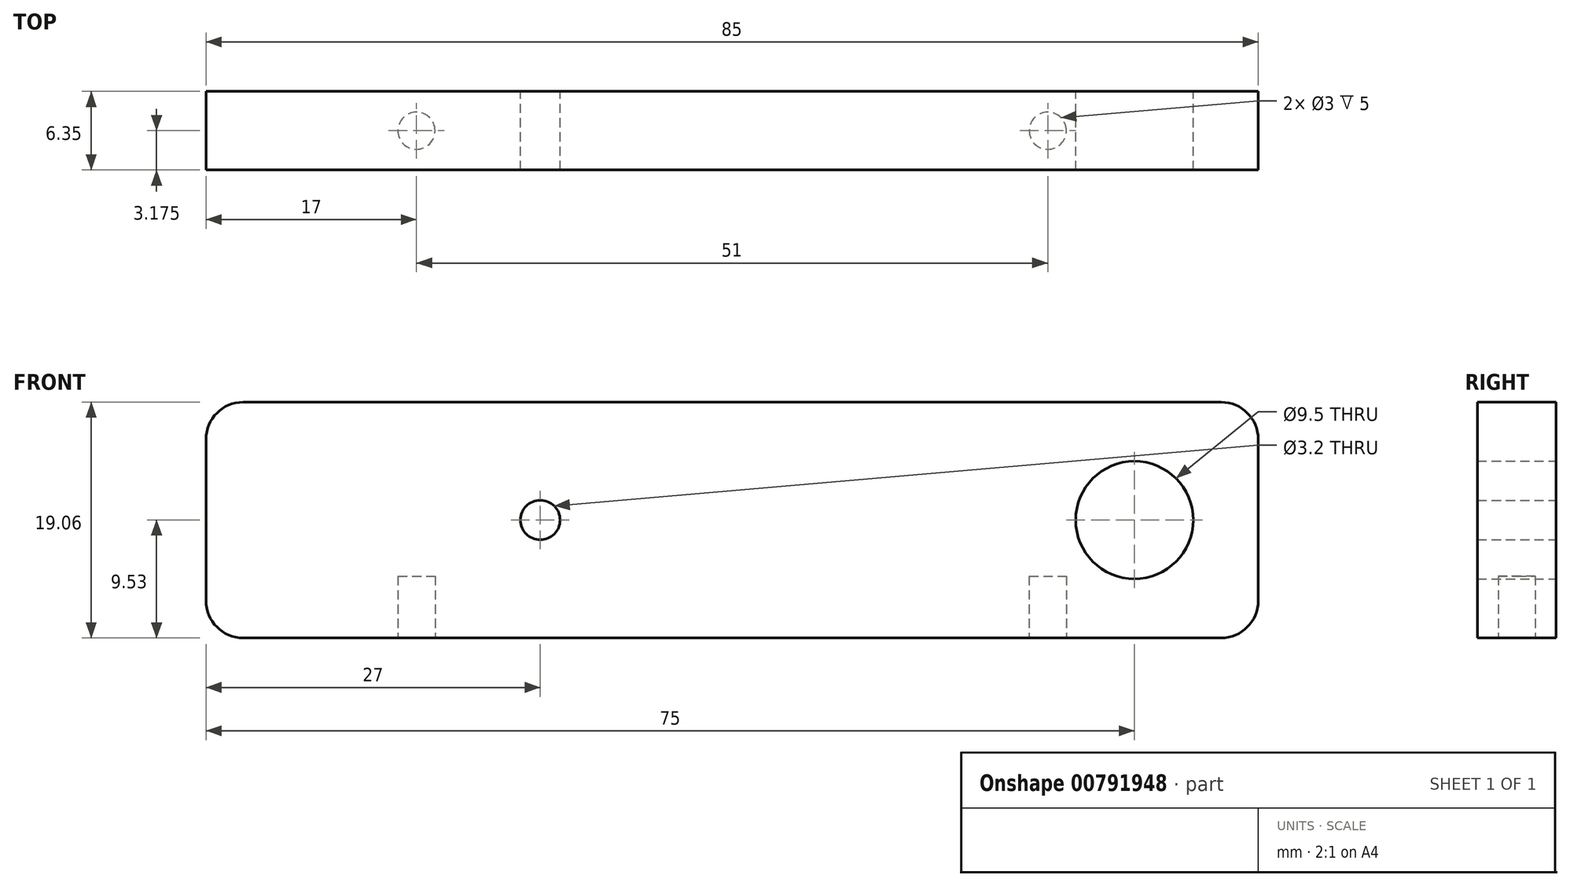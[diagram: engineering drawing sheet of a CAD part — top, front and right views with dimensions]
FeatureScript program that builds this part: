
annotation { "Feature Type Name" : "Feature", "Feature Type Description" : "" }
export const myFeature = defineFeature(function(context is Context, id is Id, definition is map)
    precondition{}
    {
        {
            var Q0;
            Q0=qCreatedBy(makeId("Front.planeOp"),FACE);
            var sketch = newSketch(context, id + "F0", { "sketchPlane" : qUnion([Q0])});
            skLineSegment(sketch, "E0.bottom", {"start": v(42.5, 9.53) * mm, "end": v(-42.5, 9.53) * mm});
            skLineSegment(sketch, "E0.top", {"start": v(42.5, -9.53) * mm, "end": v(-42.5, -9.53) * mm});
            skLineSegment(sketch, "E0.left", {"start": v(42.5, 9.53) * mm, "end": v(42.5, -9.53) * mm});
            skLineSegment(sketch, "E0.right", {"start": v(-42.5, 9.53) * mm, "end": v(-42.5, -9.53) * mm});
            skPoint(sketch, "E0.middle", {"position": v(0, 0) * mm});
            skCircle(sketch, "E1", {"center": v(32.5, 0) * mm, "radius": 4.75 * mm});
            skCircle(sketch, "E2", {"center": v(-15.5, 0) * mm, "radius": 1.6 * mm});
            skSolve(sketch);
        }
        {
            var Q0;
            Q0 = qSketchRegion(id + "F0", true);
            extrude(context, id + "F1", {"entities" : qUnion([Q0]), "depth" : 6.35 * mm, "offsetDistance" : 25 * mm});
        }
        {
            var Q0;
            Q0=makeQuery(id+"F1.opExtrude","SWEPT_FACE",FACE,{"disambiguationData":[OSD([sQuery(id+"F0.wireOp",EDGE,"E0.top")])]});
            var sketch = newSketch(context, id + "F2", { "sketchPlane" : qUnion([Q0])});
            skCircle(sketch, "E3", {"center": v(-25.5, 3.18) * mm, "radius": 1.5 * mm});
            skPoint(sketch, "E3.centerSnap0", {"position": v(-42.5, 3.17) * mm});
            skCircle(sketch, "E4.MirrorC", {"center": v(25.5, 3.18) * mm, "radius": 1.5 * mm});
            skSolve(sketch);
        }
        {
            var Q0;
            Q0 = qSketchRegion(id + "F2", true);
            extrude(context, id + "F3", {"entities" : qUnion([Q0]), "operationType" : NewBodyOperationType.REMOVE, "oppositeDirection" : true, "depth" : 5 * mm, "offsetDistance" : 25 * mm});
        }
        {
            var Q0;
            Q0=makeQuery(id+"F1.opExtrude","SWEPT_EDGE",EDGE,{"disambiguationData":[OSD([sQuery(id+"F0.wireOp",EDGE,"E0.top"),sQuery(id+"F0.wireOp",EDGE,"E0.right")])]});
            var Q1;
            Q1=makeQuery(id+"F1.opExtrude","SWEPT_EDGE",EDGE,{"disambiguationData":[OSD([sQuery(id+"F0.wireOp",EDGE,"E0.top"),sQuery(id+"F0.wireOp",EDGE,"E0.left")])]});
            var Q2;
            Q2=makeQuery(id+"F1.opExtrude","SWEPT_EDGE",EDGE,{"disambiguationData":[OSD([sQuery(id+"F0.wireOp",EDGE,"E0.bottom"),sQuery(id+"F0.wireOp",EDGE,"E0.left")])]});
            var Q3;
            Q3=makeQuery(id+"F1.opExtrude","SWEPT_EDGE",EDGE,{"disambiguationData":[OSD([sQuery(id+"F0.wireOp",EDGE,"E0.bottom"),sQuery(id+"F0.wireOp",EDGE,"E0.right")])]});
            fillet(context, id + "F4", {"entities" : qUnion([Q0, Q1, Q2, Q3]), "radius" : 3 * mm, "tangentPropagation" : true, "allowEdgeOverflow" : false});
        }
    });
